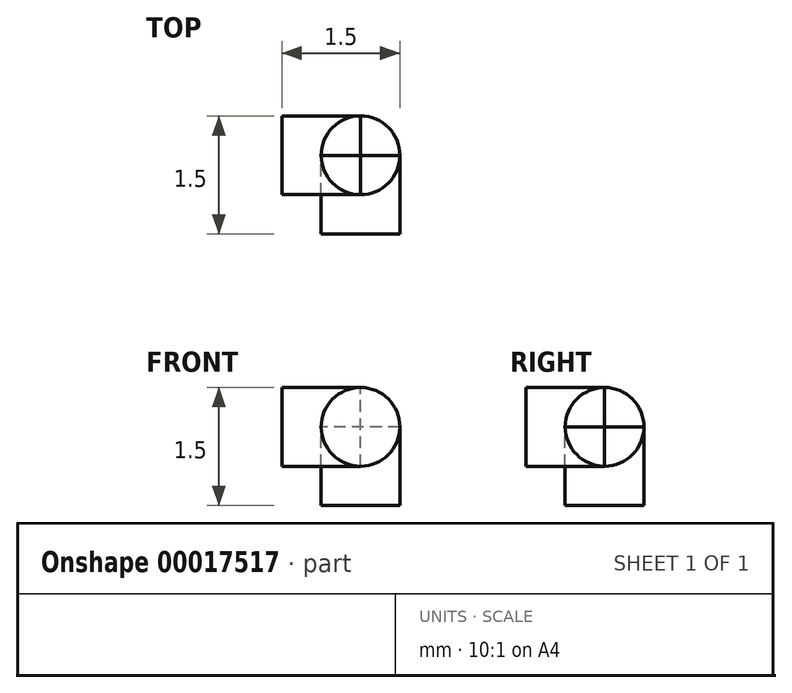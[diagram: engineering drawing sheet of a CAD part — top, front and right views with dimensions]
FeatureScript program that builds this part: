
annotation { "Feature Type Name" : "Feature", "Feature Type Description" : "" }
export const myFeature = defineFeature(function(context is Context, id is Id, definition is map)
    precondition{}
    {
        {
            var Q0;
            Q0=qCreatedBy(makeId("Right.planeOp"),FACE);
            var sketch = newSketch(context, id + "F0", { "sketchPlane" : qUnion([Q0])});
            skCircle(sketch, "E0", {"center": v(0, 0) * mm, "radius": 0.5 * mm});
            skSolve(sketch);
        }
        {
            var Q0;
            Q0 = qSketchRegion(id + "F0", true);
            extrude(context, id + "F1", {"entities" : qUnion([Q0]), "oppositeDirection" : true, "depth" : 1 * mm});
        }
        {
            var Q0;
            Q0=qCreatedBy(makeId("Front.planeOp"),FACE);
            var sketch = newSketch(context, id + "F2", { "sketchPlane" : qUnion([Q0])});
            skCircle(sketch, "E1", {"center": v(0, 0) * mm, "radius": 0.5 * mm});
            skSolve(sketch);
        }
        {
            var Q0;
            Q0 = qSketchRegion(id + "F2", true);
            extrude(context, id + "F3", {"entities" : qUnion([Q0]), "depth" : 1 * mm});
        }
        {
            var Q0;
            Q0=qCreatedBy(makeId("Top.planeOp"),FACE);
            var sketch = newSketch(context, id + "F4", { "sketchPlane" : qUnion([Q0])});
            skCircle(sketch, "E2", {"center": v(0, 0) * mm, "radius": 0.5 * mm});
            skSolve(sketch);
        }
        {
            var Q0;
            Q0 = qSketchRegion(id + "F4", true);
            extrude(context, id + "F5", {"entities" : qUnion([Q0]), "oppositeDirection" : true, "depth" : 1 * mm});
        }
    });
